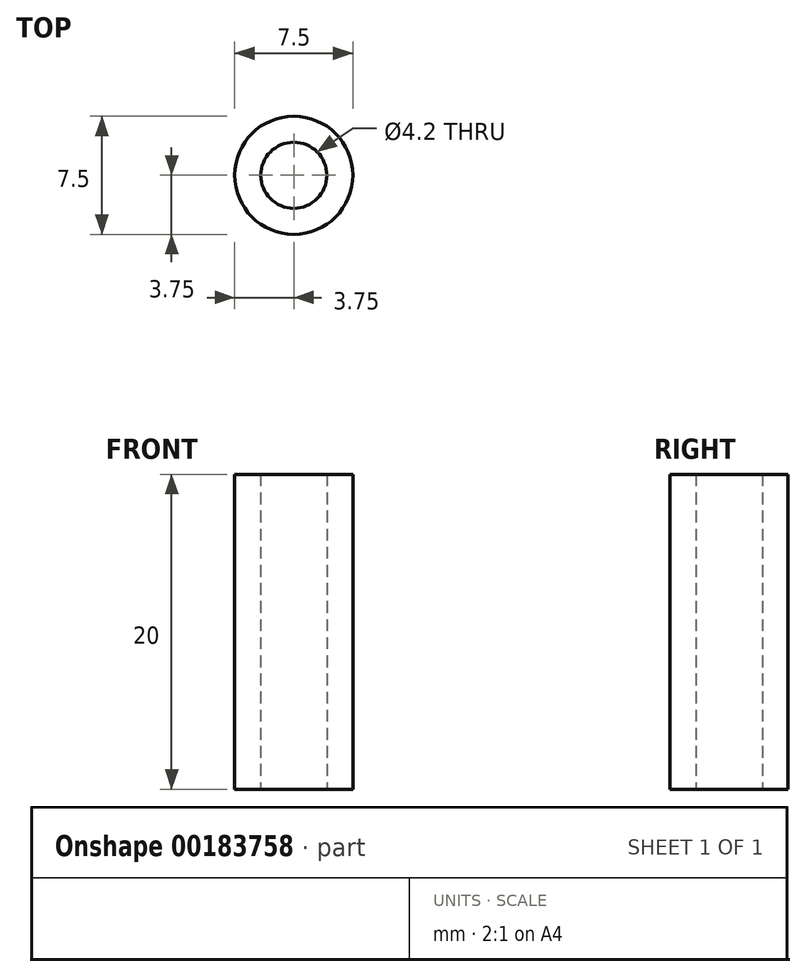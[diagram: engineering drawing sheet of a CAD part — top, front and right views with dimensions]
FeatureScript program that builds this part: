
annotation { "Feature Type Name" : "Feature", "Feature Type Description" : "" }
export const myFeature = defineFeature(function(context is Context, id is Id, definition is map)
    precondition{}
    {
        {
            var Q0;
            Q0=qCreatedBy(makeId("Top.planeOp"),FACE);
            var sketch = newSketch(context, id + "F0", { "sketchPlane" : qUnion([Q0])});
            skCircle(sketch, "E0", {"center": v(0, 0) * mm, "radius": 3.75 * mm});
            skCircle(sketch, "E1", {"center": v(0, 0) * mm, "radius": 2.1 * mm});
            skSolve(sketch);
        }
        {
            var Q0;
            Q0=makeQuery(id+"F0.imprint","IMPRINT",FACE,{"disambiguationData":[TD([[makeQuery(id+"F0.imprint","IMPRINT",EDGE,{"derivedFrom":sQuery(id+"F0.wireOp",EDGE,"E0")}),1.0]])]});
            extrude(context, id + "F1", {"entities" : qUnion([Q0]), "depth" : 20 * mm});
        }
    });
